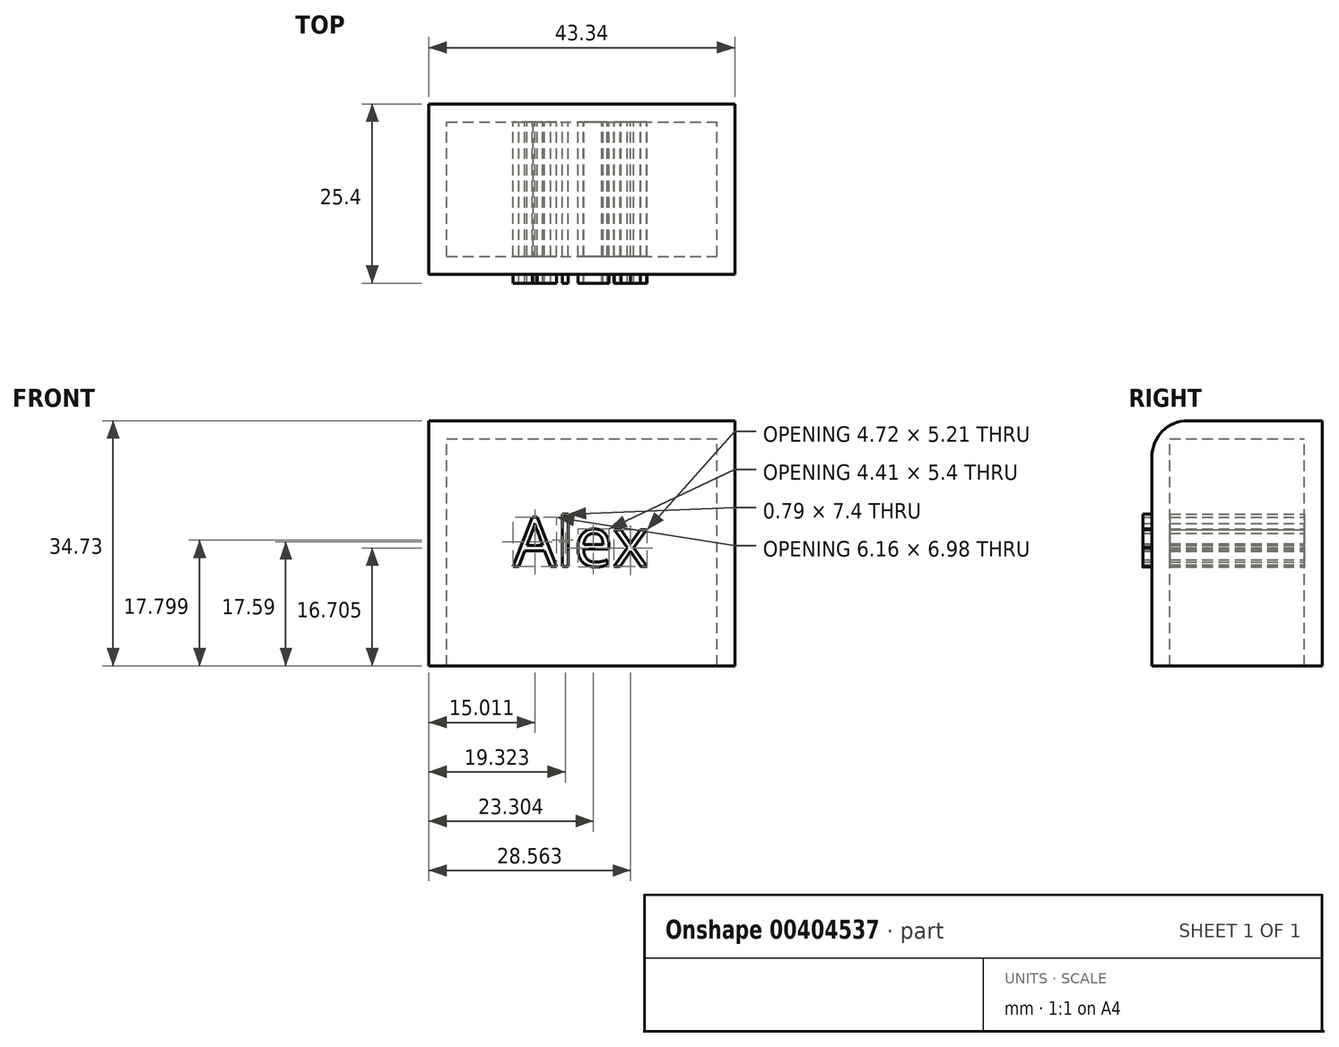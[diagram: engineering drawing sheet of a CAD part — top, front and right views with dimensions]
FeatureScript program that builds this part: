
annotation { "Feature Type Name" : "Feature", "Feature Type Description" : "" }
export const myFeature = defineFeature(function(context is Context, id is Id, definition is map)
    precondition{}
    {
        {
            var Q0;
            Q0=qCreatedBy(makeId("Front.planeOp"),FACE);
            var sketch = newSketch(context, id + "F0", { "sketchPlane" : qUnion([Q0])});
            skLineSegment(sketch, "E0.bottom", {"start": v(-21.57, 0) * mm, "end": v(21.77, 0) * mm});
            skLineSegment(sketch, "E0.top", {"start": v(-21.57, 34.73) * mm, "end": v(21.77, 34.73) * mm});
            skLineSegment(sketch, "E0.left", {"start": v(-21.57, 0) * mm, "end": v(-21.57, 34.73) * mm});
            skLineSegment(sketch, "E0.right", {"start": v(21.77, 0) * mm, "end": v(21.77, 34.73) * mm});
            skSolve(sketch);
        }
        {
            var Q0;
            Q0=makeQuery(id+"F0.imprint","IMPRINT",FACE,{"disambiguationData":[TD([[makeQuery(id+"F0.imprint","IMPRINT",EDGE,{"derivedFrom":sQuery(id+"F0.wireOp",EDGE,"E0.bottom")}),1.0]])]});
            extrude(context, id + "F1", {"entities" : qUnion([Q0]), "depth" : 24.13 * mm});
        }
        {
            var Q0;
            Q0=makeQuery(id+"F1.opExtrude","SWEPT_FACE",FACE,{"disambiguationData":[OSD([sQuery(id+"F0.wireOp",EDGE,"E0.bottom")])]});
            shell(context, id + "F2", {"entities" : qUnion([Q0]), "thickness" : 2.54 * mm});
        }
        {
            var Q0;
            Q0=makeQuery(id+"F1.opExtrude","CAP_EDGE",EDGE,{"disambiguationData":[OSD([sQuery(id+"F0.wireOp",EDGE,"E0.top")])],"isStart":false});
            fillet(context, id + "F3", {"entities" : qUnion([Q0]), "radius" : 5.08 * mm, "tangentPropagation" : true, "allowEdgeOverflow" : false});
        }
        {
            var Q0;
            Q0=qCreatedBy(makeId("Front.planeOp"),FACE);
            var sketch = newSketch(context, id + "F4", { "sketchPlane" : qUnion([Q0])});
            skText(sketch, "E1", { "text": "Alex", "fontName": "OpenSans-Regular.ttf"});
            const initialGuessF4  = {"E1": [-0.00964, 0.0141, 1, 0, 0.00701]};
            skSetInitialGuess(sketch, initialGuessF4);
            skSolve(sketch);
        }
        {
            var Q0;
            Q0 = qSketchRegion(id + "F4", true);
            extrude(context, id + "F5", {"entities" : qUnion([Q0]), "operationType" : NewBodyOperationType.ADD, "depth" : 25.4 * mm});
        }
    });
